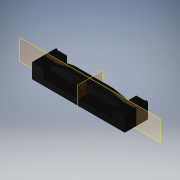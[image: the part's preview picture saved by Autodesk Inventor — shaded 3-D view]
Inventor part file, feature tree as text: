
AUTODESK INVENTOR PART (.ipt)
format: ipt  version: 2019 (Build 230136000, 136)  size: 235,520 bytes
history: native  units: mm (DEFAULTED — no unit token found)
features: sketch x8, extrude x5, fillet x1
ambient origin geometry x8: Origin, YZ Plane, XZ Plane, XY Plane, X Axis, Y Axis, Z Axis, Center Point
bodies: Solid1 (feature_tree)
feature tree (14):
  extrude  "Extrusion1"  Depth=10.0mm
  extrude  "Extrusion2"  Depth=40.0mm
  extrude  "Extrusion3"  Depth=0.5842mm TaperAngle=0.0deg
  extrude  "Extrusion4"  Depth=2.54mm
  extrude  "Extrusion5"  Depth=1.3208mm
  fillet  "Fillet1"  Radius=0.762mm
  sketch  "Sketch8"  dims[d15=8.128mm]
  sketch  "Sketch9"  dims[d16=16.891mm]
  sketch  "Sketch11"  dims[d17=0.508mm d18=3.302mm d19=0.0mm d20=1.143mm d21=3.302mm d22=0.0mm d23=0.5842mm d37=0.508mm d38=0.5842mm d39=0.254mm d40=160.0mm d42=1.27mm d43=10.0mm d45=25.4mm d48=1.27mm d49=1.27mm d50=1.27mm d51=1.27mm d53=1.27mm d54=1.27mm d55=1.27mm d56=1.27mm d57=1.27mm d58=1.27mm d59=1.27mm d60=1.27mm d61=1.27mm d62=1.27mm d64=0.4318mm d65=2.032mm d66=1.27mm d67=0.4318mm d68=0.4318mm d69=1.27mm d70=20.0mm d72=22.86mm d73=10.0mm d75=25.4mm d77=20.0mm d79=1.3843mm d80=10.0mm d82=25.4mm d84=20.0mm d86=1.016mm d87=10.0mm d89=25.4mm d91=20.0mm d93=1.016mm d94=10.0mm d96=25.4mm]
  sketch  "Sketch1"  dims[d0=40.0mm d1=10.0mm]
  sketch  "Sketch2"  dims[d2=7.4676mm d3=0.0mm d4=40.0mm]
  sketch  "Sketch3"  dims[d5=0.5842mm d6=7.4676mm d7=0.0mm]
  sketch  "Sketch4"  dims[d8=30.0mm d9=2.54mm]
  sketch  "Sketch5"  dims[d11=7.4676mm d12=0.0mm d13=1.3208mm d14=0.762mm]
